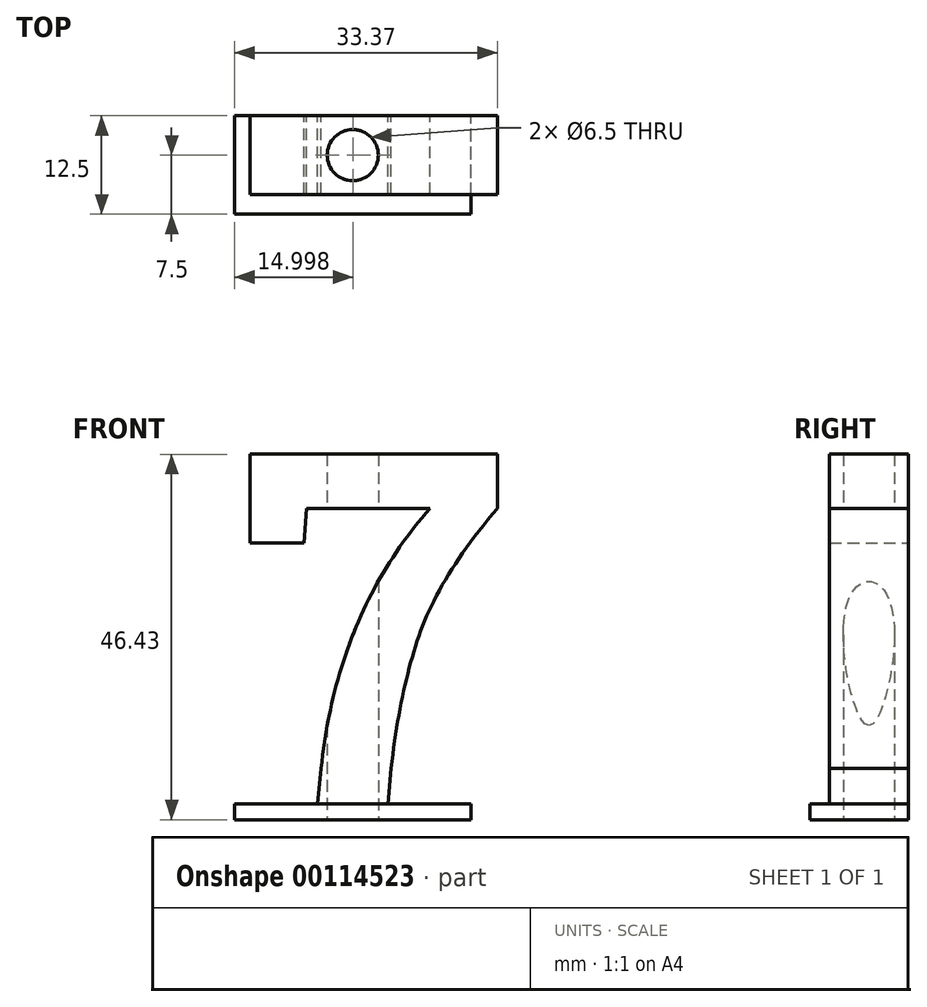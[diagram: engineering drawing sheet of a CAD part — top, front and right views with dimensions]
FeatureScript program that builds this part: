
annotation { "Feature Type Name" : "Feature", "Feature Type Description" : "" }
export const myFeature = defineFeature(function(context is Context, id is Id, definition is map)
    precondition{}
    {
        {
            var Q0;
            Q0=qCreatedBy(makeId("Front.planeOp"),FACE);
            var sketch = newSketch(context, id + "F0", { "sketchPlane" : qUnion([Q0])});
            skText(sketch, "E0", { "text": "7", "fontName": "RobotoSlab-Bold.ttf"});
            const initialGuessF0  = {"E0": [-0.01993, 0, 1, 0, 0.045]};
            skSetInitialGuess(sketch, initialGuessF0);
            skSolve(sketch);
        }
        {
            var Q0;
            Q0 = qSketchRegion(id + "F0", true);
            extrude(context, id + "F1", {"entities" : qUnion([Q0]), "depth" : 5 * mm});
        }
        {
            var Q0;
            Q0=makeQuery(id+"F1.opExtrude","CAP_FACE",FACE,{"disambiguationData":[OSD([sQuery(id+"F0.wireOp",EDGE,"E0.sketch_text.stroke-0"),sQuery(id+"F0.wireOp",EDGE,"E0.sketch_text.stroke-1"),sQuery(id+"F0.wireOp",EDGE,"E0.sketch_text.stroke-2"),sQuery(id+"F0.wireOp",EDGE,"E0.sketch_text.stroke-3"),sQuery(id+"F0.wireOp",EDGE,"E0.sketch_text.stroke-4"),sQuery(id+"F0.wireOp",EDGE,"E0.sketch_text.stroke-5"),sQuery(id+"F0.wireOp",EDGE,"E0.sketch_text.stroke-6"),sQuery(id+"F0.wireOp",EDGE,"E0.sketch_text.stroke-7"),sQuery(id+"F0.wireOp",EDGE,"E0.sketch_text.stroke-8"),sQuery(id+"F0.wireOp",EDGE,"E0.sketch_text.stroke-9"),sQuery(id+"F0.wireOp",EDGE,"E0.sketch_text.stroke-10"),sQuery(id+"F0.wireOp",EDGE,"E0.sketch_text.stroke-11"),sQuery(id+"F0.wireOp",EDGE,"E0.sketch_text.stroke-12")])],"isStart":true});
            extrude(context, id + "F2", {"entities" : qUnion([Q0]), "operationType" : NewBodyOperationType.ADD, "depth" : 5 * mm});
        }
        {
            var Q0;
            {var subQ0=sQuery(id+"F0.wireOp",EDGE,"E0.sketch_text.stroke-3");Q0=makeQuery(id+"F2.boolean.opBoolean","MERGE",FACE,{"derivedFrom":[makeQuery(id+"F1.opExtrude","SWEPT_FACE",FACE,{"disambiguationData":[OSD([subQ0])]}),makeQuery(id+"F2.opExtrude","SWEPT_FACE",FACE,{"disambiguationData":[OSD([subQ0])]})]});}
            var sketch = newSketch(context, id + "F3", { "sketchPlane" : qUnion([Q0])});
            skLineSegment(sketch, "E1.bottom", {"start": v(9.6, 7.5) * mm, "end": v(-20.4, 7.5) * mm});
            skLineSegment(sketch, "E1.top", {"start": v(9.6, -7.5) * mm, "end": v(-20.4, -7.5) * mm});
            skLineSegment(sketch, "E1.left", {"start": v(9.6, 7.5) * mm, "end": v(9.6, -7.5) * mm});
            skLineSegment(sketch, "E1.right", {"start": v(-20.4, 7.5) * mm, "end": v(-20.4, -7.5) * mm});
            skPoint(sketch, "E1.middle", {"position": v(-5.4, 0) * mm});
            skPoint(sketch, "E1.middle.positionSnap0", {"position": v(-5.4, 5) * mm});
            skPoint(sketch, "E1.middle.positionSnap1", {"position": v(-9.86, 0) * mm});
            skPoint(sketch, "E1.centerSnap0", {"position": v(-5.4, 5) * mm});
            skPoint(sketch, "E1.centerSnap1", {"position": v(-9.86, 0) * mm});
            skSolve(sketch);
        }
        {
            var Q0;
            Q0=makeQuery(id+"F3.imprint","IMPRINT",FACE,{"disambiguationData":[TD([[makeQuery(id+"F3.imprint","IMPRINT",EDGE,{"derivedFrom":sQuery(id+"F3.wireOp",EDGE,"E1.bottom")}),1.0]])]});
            extrude(context, id + "F4", {"entities" : qUnion([Q0]), "depth" : 2 * mm});
        }
        {
            var Q0;
            {var subQ0=sQuery(id+"F0.wireOp",EDGE,"E0.sketch_text.stroke-3");Q0=makeQuery(id+"F2.boolean.opBoolean","MERGE",FACE,{"derivedFrom":[makeQuery(id+"F1.opExtrude","SWEPT_FACE",FACE,{"disambiguationData":[OSD([subQ0])]}),makeQuery(id+"F2.opExtrude","SWEPT_FACE",FACE,{"disambiguationData":[OSD([subQ0])]})]});}
            var sketch = newSketch(context, id + "F5", { "sketchPlane" : qUnion([Q0])});
            skCircle(sketch, "E2", {"center": v(-5.4, 0) * mm, "radius": 3.25 * mm});
            skPoint(sketch, "E2.centerSnap0", {"position": v(-5.4, 5) * mm});
            skPoint(sketch, "E2.centerSnap1", {"position": v(-9.86, 0) * mm});
            skSolve(sketch);
        }
        {
            var Q0;
            Q0=makeQuery(id+"F5.imprint","IMPRINT",FACE,{"disambiguationData":[TD([[makeQuery(id+"F5.imprint","IMPRINT",EDGE,{"derivedFrom":sQuery(id+"F5.wireOp",EDGE,"E2")}),1.0]])]});
            extrude(context, id + "F6", {"entities" : qUnion([Q0]), "operationType" : NewBodyOperationType.REMOVE, "endBound" : BoundingType.THROUGH_ALL, "oppositeDirection" : true, "depth" : 25 * mm});
        }
        {
            var Q0;
            {var subQ0=sQuery(id+"F0.wireOp",EDGE,"E0.sketch_text.stroke-3");Q0=makeQuery(id+"F2.boolean.opBoolean","MERGE",FACE,{"derivedFrom":[makeQuery(id+"F1.opExtrude","SWEPT_FACE",FACE,{"disambiguationData":[OSD([subQ0])]}),makeQuery(id+"F2.opExtrude","SWEPT_FACE",FACE,{"disambiguationData":[OSD([subQ0])]})]});}
            extrude(context, id + "F7", {"entities" : qUnion([Q0]), "operationType" : NewBodyOperationType.ADD, "depth" : 2 * mm});
        }
        {
            var Q0;
            Q0=makeQuery(id+"F4.opExtrude","SWEPT_FACE",FACE,{"disambiguationData":[OSD([sQuery(id+"F3.wireOp",EDGE,"E1.top")])]});
            extrude(context, id + "F8", {"entities" : qUnion([Q0]), "operationType" : NewBodyOperationType.REMOVE, "oppositeDirection" : true, "depth" : 2.5 * mm});
        }
    });
